# Revit family: 879-100X99-001-DN50-600
name_source: partatom
category: Pipe Accessories
units: mm (PartAtom-declared; Revit-internal decimal feet)

## family parameters
Always vertical = Yes
Cut with Voids When Loaded = No
Part Type = Valve - Breaks Into
Round Connector Dimension = Use Diameter
Shared = No
Work Plane-Based = No

## types (42) — shared parameters
879-0065-10-14400059999 = DN65_PN10/16
879-0065-10-144000599A0 = DN65_PN10/16
879-0080-10-14400059999 = DN80_PN10/16
879-0080-10-144000599A0 = DN80_PN10/16
879-0100-10-14400059999 = DN100_PN10/16
879-0100-10-144000599A0 = DN100_PN10/16
879-0150-10-14400059999 = DN150_PN10/16
879-0150-10-144000599A0 = DN150_PN10/16
879-0200-10-04400059999 = DN200_PN10
879-0200-10-044000599A0 = DN200_PN10
879-0200-10-14400059999 = DN200_PN16
879-0200-10-144000599A0 = DN200_PN16
879-0250-10-04400059999 = DN250_PN10
879-0250-10-044000599A0 = DN250_PN10
879-0250-10-14400059999 = DN250_PN16
879-0250-10-144000599A0 = DN250_PN16
879-0300-10-04400059999 = DN300_PN10
879-0300-10-044000599A0 = DN300_PN10
879-0300-10-14400059999 = DN300_PN16
879-0300-10-144000599A0 = DN300_PN16
879-0350-10-04400059999 = DN350_PN10
879-0350-10-044000599A0 = DN350_PN10
879-0350-10-14400059999 = DN350_PN16
879-0350-10-144000599A0 = DN350_PN16
879-0400-10-04400059999 = DN400_PN10
879-0400-10-044000599A0 = DN400_PN10
879-0400-10-14400059999 = DN400_PN16
879-0400-10-144000599A0 = DN400_PN16
879-0450-10-04400059999 = DN450_PN10
879-0450-10-044000599A0 = DN450_PN10
879-0450-10-14400059999 = DN450_PN16
879-0450-10-144000599A0 = DN450_PN16
879-0500-10-04400059999 = DN500_PN10
879-0500-10-044000599A0 = DN500_PN10
879-0500-10-14400059999 = DN500_PN16
879-0500-10-144000599A0 = DN500_PN16
879-0600-10-04400059999 = DN600_PN10
879-0600-10-044000599A0 = DN600_PN10
879-0600-10-14400059999 = DN600_PN16
879-0600-10-144000599A0 = DN600_PN16
Body_wall_thickness = 10 mm  [stored 0.0328084 ft]
Description_ = AVK PRESSURE REDUCING CONTROL VALVE
Search_Table = 879-100X99-001-DN50-600
URL product pages = https://www.avkvalves.com

## per-type parameters (varying)
- 879-0065-10-14400059999_DN65_PN10/16: 879-0050-10-14400059999=DN50_PN10/16; 879-0050-10-144000599A0=DN50_PN10/16; Body_Collar_Dia=30 mm  [stored 0.0984252 ft]; Body_Collar_Dia_2=26 mm; Body_Flange_Dia=94 mm; Body_Flange_Dia_2=104 mm; Body_Height_1=73 mm; Body_Height_2=36 mm  [stored 0.11811 ft]; Body_Height_3=58 mm; Body_Height_4=51 mm; Body_Top_Dia=13 mm; Body_Top_Dia_2=11 mm; Body_With_Dia=73 mm; Body_With_Dia_2=78 mm; Bolt_support=193 mm; Bolt_support_2=97 mm; Bolt_support_Dia=12 mm  [stored 0.0393701 ft]; Bolt_support_lenght=53 mm; Bolt_support_lenght_2=63 mm; Bottom_profile=16 mm  [stored 0.0524934 ft]; D1=59 mm; D3=93 mm; DN=65 mm; Fillet_Length=6 mm  [stored 0.019685 ft]; Flange_thickness=19 mm  [stored 0.062336 ft]; H3=395 mm; ID=33 mm; L=290 mm; PG_Dia=33 mm; PG_Ref=48 mm; PG_depth=8 mm  [stored 0.0262467 ft]; PG_ref=43 mm; Pilot_Dia_1=18 mm; Pilot_Dia_2=35 mm  [stored 0.114829 ft]; Pilot_Dia_3=12 mm  [stored 0.0393701 ft]; Pilot_Dia_4=6 mm  [stored 0.019685 ft]; Pilot_Dia_5=4 mm  [stored 0.0131234 ft]; Pilot_top_1=252 mm; Pilot_top_ref=50 mm; Profile1_Height=152 mm; Profile1_Length=25 mm  [stored 0.082021 ft]; Profile1_Length_2=17 mm; Profile_Dia=6 mm  [stored 0.019685 ft]; Profile_Dia_2=6 mm  [stored 0.019685 ft]; Profile_Dia_3=12 mm  [stored 0.0393701 ft]; Top_Profile=116 mm; Top_Profile_Ref=121 mm; W=285 mm; W_Ref=281 mm
- 879-0065-10-144000599A0_DN65_PN10/16: 879-0050-10-14400059999=DN50_PN10/16; 879-0050-10-144000599A0=DN50_PN10/16; Body_Collar_Dia=30 mm  [stored 0.0984252 ft]; Body_Collar_Dia_2=26 mm; Body_Flange_Dia=94 mm; Body_Flange_Dia_2=104 mm; Body_Height_1=73 mm; Body_Height_2=36 mm  [stored 0.11811 ft]; Body_Height_3=73 mm; Body_Height_4=51 mm; Body_Top_Dia=13 mm; Body_Top_Dia_2=11 mm; Body_With_Dia=73 mm; Body_With_Dia_2=78 mm; Bolt_support=193 mm; Bolt_support_2=97 mm; Bolt_support_Dia=12 mm  [stored 0.0393701 ft]; Bolt_support_lenght=53 mm; Bolt_support_lenght_2=63 mm; Bottom_profile=16 mm  [stored 0.0524934 ft]; D1=59 mm; D3=93 mm; DN=65 mm; Fillet_Length=6 mm  [stored 0.019685 ft]; Flange_thickness=19 mm  [stored 0.062336 ft]; H3=436 mm; ID=33 mm; L=290 mm; PG_Dia=33 mm; PG_Ref=48 mm; PG_depth=8 mm  [stored 0.0262467 ft]; PG_ref=43 mm; Pilot_Dia_1=18 mm; Pilot_Dia_2=35 mm  [stored 0.114829 ft]; Pilot_Dia_3=12 mm  [stored 0.0393701 ft]; Pilot_Dia_4=6 mm  [stored 0.019685 ft]; Pilot_Dia_5=4 mm  [stored 0.0131234 ft]; Pilot_top_1=280 mm; Pilot_top_ref=64 mm; Profile1_Height=170 mm; Profile1_Length=25 mm  [stored 0.082021 ft]; Profile1_Length_2=17 mm; Profile_Dia=6 mm  [stored 0.019685 ft]; Profile_Dia_2=6 mm  [stored 0.019685 ft]; Profile_Dia_3=12 mm  [stored 0.0393701 ft]; Top_Profile=116 mm; Top_Profile_Ref=121 mm; W=285 mm; W_Ref=281 mm
- 879-0080-10-14400059999_DN80_PN10/16: 879-0050-10-14400059999=DN50_PN10/16; 879-0050-10-144000599A0=DN50_PN10/16; Body_Collar_Dia=32 mm; Body_Collar_Dia_2=28 mm  [stored 0.0918635 ft]; Body_Flange_Dia=100 mm; Body_Flange_Dia_2=111 mm; Body_Height_1=78 mm; Body_Height_2=39 mm  [stored 0.127953 ft]; Body_Height_3=62 mm; Body_Height_4=54 mm; Body_Top_Dia=14 mm  [stored 0.0459318 ft]; Body_Top_Dia_2=12 mm  [stored 0.0393701 ft]; Body_With_Dia=78 mm; Body_With_Dia_2=84 mm; Bolt_support=207 mm; Bolt_support_2=103 mm; Bolt_support_Dia=12 mm  [stored 0.0393701 ft]; Bolt_support_lenght=60 mm; Bolt_support_lenght_2=70 mm; Bottom_profile=20 mm  [stored 0.0656168 ft]; D1=66 mm; D3=100 mm; DN=80 mm; Fillet_Length=6 mm  [stored 0.019685 ft]; Flange_thickness=19 mm  [stored 0.062336 ft]; H3=410 mm; ID=40 mm  [stored 0.131234 ft]; L=310 mm; PG_Dia=40 mm  [stored 0.131234 ft]; PG_Ref=52 mm; PG_depth=8 mm  [stored 0.0262467 ft]; PG_ref=50 mm; Pilot_Dia_1=20 mm  [stored 0.0656168 ft]; Pilot_Dia_2=39 mm  [stored 0.127953 ft]; Pilot_Dia_3=13 mm; Pilot_Dia_4=7 mm; Pilot_Dia_5=4 mm  [stored 0.0131234 ft]; Pilot_top_1=262 mm; Pilot_top_ref=48 mm; Profile1_Height=179 mm; Profile1_Length=27 mm  [stored 0.0885827 ft]; Profile1_Length_2=18 mm; Profile_Dia=6 mm  [stored 0.019685 ft]; Profile_Dia_2=6 mm  [stored 0.019685 ft]; Profile_Dia_3=12 mm  [stored 0.0393701 ft]; Top_Profile=124 mm; Top_Profile_Ref=129 mm; W=300 mm; W_Ref=296 mm
- 879-0080-10-144000599A0_DN80_PN10/16: 879-0050-10-14400059999=DN50_PN10/16; 879-0050-10-144000599A0=DN50_PN10/16; Body_Collar_Dia=32 mm; Body_Collar_Dia_2=28 mm  [stored 0.0918635 ft]; Body_Flange_Dia=100 mm; Body_Flange_Dia_2=111 mm; Body_Height_1=78 mm; Body_Height_2=39 mm  [stored 0.127953 ft]; Body_Height_3=78 mm; Body_Height_4=54 mm; Body_Top_Dia=14 mm  [stored 0.0459318 ft]; Body_Top_Dia_2=12 mm  [stored 0.0393701 ft]; Body_With_Dia=78 mm; Body_With_Dia_2=84 mm; Bolt_support=207 mm; Bolt_support_2=103 mm; Bolt_support_Dia=12 mm  [stored 0.0393701 ft]; Bolt_support_lenght=60 mm; Bolt_support_lenght_2=70 mm; Bottom_profile=20 mm  [stored 0.0656168 ft]; D1=66 mm; D3=100 mm; DN=80 mm; Fillet_Length=6 mm  [stored 0.019685 ft]; Flange_thickness=19 mm  [stored 0.062336 ft]; H3=451 mm; ID=40 mm  [stored 0.131234 ft]; L=310 mm; PG_Dia=40 mm  [stored 0.131234 ft]; PG_Ref=52 mm; PG_depth=8 mm  [stored 0.0262467 ft]; PG_ref=50 mm; Pilot_Dia_1=20 mm  [stored 0.0656168 ft]; Pilot_Dia_2=39 mm  [stored 0.127953 ft]; Pilot_Dia_3=13 mm; Pilot_Dia_4=7 mm; Pilot_Dia_5=4 mm  [stored 0.0131234 ft]; Pilot_top_1=290 mm; Pilot_top_ref=61 mm; Profile1_Height=168 mm; Profile1_Length=27 mm  [stored 0.0885827 ft]; Profile1_Length_2=18 mm; Profile_Dia=6 mm  [stored 0.019685 ft]; Profile_Dia_2=6 mm  [stored 0.019685 ft]; Profile_Dia_3=12 mm  [stored 0.0393701 ft]; Top_Profile=124 mm; Top_Profile_Ref=129 mm; W=300 mm; W_Ref=296 mm
- 879-0100-10-14400059999_DN100_PN10/16: 879-0050-10-14400059999=DN50_PN10/16; 879-0050-10-144000599A0=DN50_PN10/16; Body_Collar_Dia=36 mm  [stored 0.11811 ft]; Body_Collar_Dia_2=31 mm  [stored 0.101706 ft]; Body_Flange_Dia=113 mm; Body_Flange_Dia_2=125 mm; Body_Height_1=88 mm; Body_Height_2=44 mm; Body_Height_3=59 mm; Body_Height_4=59 mm; Body_Top_Dia=16 mm  [stored 0.0524934 ft]; Body_Top_Dia_2=13 mm; Body_With_Dia=88 mm; Body_With_Dia_2=95 mm; Bolt_support=233 mm; Bolt_support_2=117 mm; Bolt_support_Dia=12 mm  [stored 0.0393701 ft]; Bolt_support_lenght=70 mm; Bolt_support_lenght_2=80 mm; Bottom_profile=25 mm  [stored 0.082021 ft]; D1=78 mm; D3=110 mm; DN=100 mm; Fillet_Length=6 mm  [stored 0.019685 ft]; Flange_thickness=19 mm  [stored 0.062336 ft]; H3=430 mm; ID=50 mm; L=350 mm; PG_Dia=50 mm; PG_Ref=58 mm; PG_depth=8 mm  [stored 0.0262467 ft]; PG_ref=60 mm; Pilot_Dia_1=22 mm  [stored 0.0721785 ft]; Pilot_Dia_2=44 mm; Pilot_Dia_3=15 mm  [stored 0.0492126 ft]; Pilot_Dia_4=7 mm; Pilot_Dia_5=5 mm  [stored 0.0164042 ft]; Pilot_top_1=272 mm; Pilot_top_ref=48 mm; Profile1_Height=185 mm; Profile1_Length=30 mm  [stored 0.0984252 ft]; Profile1_Length_2=20 mm  [stored 0.0656168 ft]; Profile_Dia=6 mm  [stored 0.019685 ft]; Profile_Dia_2=6 mm  [stored 0.019685 ft]; Profile_Dia_3=12 mm  [stored 0.0393701 ft]; Top_Profile=140 mm; Top_Profile_Ref=145 mm; W=320 mm; W_Ref=316 mm
- 879-0100-10-144000599A0_DN100_PN10/16: 879-0050-10-14400059999=DN50_PN10/16; 879-0050-10-144000599A0=DN50_PN10/16; Body_Collar_Dia=36 mm  [stored 0.11811 ft]; Body_Collar_Dia_2=31 mm  [stored 0.101706 ft]; Body_Flange_Dia=113 mm; Body_Flange_Dia_2=125 mm; Body_Height_1=88 mm; Body_Height_2=44 mm; Body_Height_3=70 mm; Body_Height_4=59 mm; Body_Top_Dia=16 mm  [stored 0.0524934 ft]; Body_Top_Dia_2=13 mm; Body_With_Dia=88 mm; Body_With_Dia_2=95 mm; Bolt_support=233 mm; Bolt_support_2=117 mm; Bolt_support_Dia=12 mm  [stored 0.0393701 ft]; Bolt_support_lenght=70 mm; Bolt_support_lenght_2=80 mm; Bottom_profile=25 mm  [stored 0.082021 ft]; D1=78 mm; D3=110 mm; DN=100 mm; Fillet_Length=6 mm  [stored 0.019685 ft]; Flange_thickness=19 mm  [stored 0.062336 ft]; H3=474 mm; ID=50 mm; L=350 mm; PG_Dia=50 mm; PG_Ref=58 mm; PG_depth=8 mm  [stored 0.0262467 ft]; PG_ref=60 mm; Pilot_Dia_1=22 mm  [stored 0.0721785 ft]; Pilot_Dia_2=44 mm; Pilot_Dia_3=15 mm  [stored 0.0492126 ft]; Pilot_Dia_4=7 mm; Pilot_Dia_5=5 mm  [stored 0.0164042 ft]; Pilot_top_1=300 mm; Pilot_top_ref=64 mm; Profile1_Height=176 mm; Profile1_Length=30 mm  [stored 0.0984252 ft]; Profile1_Length_2=20 mm  [stored 0.0656168 ft]; Profile_Dia=6 mm  [stored 0.019685 ft]; Profile_Dia_2=6 mm  [stored 0.019685 ft]; Profile_Dia_3=12 mm  [stored 0.0393701 ft]; Top_Profile=140 mm; Top_Profile_Ref=145 mm; W=320 mm; W_Ref=316 mm
- 879-0150-10-14400059999_DN150_PN10/16: 879-0050-10-14400059999=DN50_PN10/16; 879-0050-10-144000599A0=DN50_PN10/16; Body_Collar_Dia=50 mm; Body_Collar_Dia_2=43 mm; Body_Flange_Dia=155 mm; Body_Flange_Dia_2=171 mm; Body_Height_1=120 mm; Body_Height_2=60 mm; Body_Height_3=60 mm; Body_Height_4=75 mm; Body_Top_Dia=22 mm  [stored 0.0721785 ft]; Body_Top_Dia_2=18 mm; Body_With_Dia=120 mm; Body_With_Dia_2=130 mm; Bolt_support=320 mm; Bolt_support_2=160 mm; Bolt_support_Dia=16 mm  [stored 0.0524934 ft]; Bolt_support_lenght=95 mm; Bolt_support_lenght_2=105 mm; Bottom_profile=38 mm; D1=106 mm; D3=143 mm; DN=150 mm; Fillet_Length=8 mm  [stored 0.0262467 ft]; Flange_thickness=19 mm  [stored 0.062336 ft]; H3=575 mm; ID=75 mm; L=480 mm; PG_Dia=50 mm; PG_Ref=80 mm; PG_depth=11 mm; PG_ref=85 mm; Pilot_Dia_1=31 mm  [stored 0.101706 ft]; Pilot_Dia_2=62 mm; Pilot_Dia_3=21 mm  [stored 0.0688976 ft]; Pilot_Dia_4=10 mm  [stored 0.0328084 ft]; Pilot_Dia_5=7 mm; Pilot_top_1=354 mm; Pilot_top_ref=79 mm; Profile1_Height=230 mm; Profile1_Length=39 mm  [stored 0.127953 ft]; Profile1_Length_2=26 mm; Profile_Dia=8 mm  [stored 0.0262467 ft]; Profile_Dia_2=8 mm  [stored 0.0262467 ft]; Profile_Dia_3=16 mm  [stored 0.0524934 ft]; Top_Profile=192 mm; Top_Profile_Ref=197 mm; W=385 mm; W_Ref=379 mm
- 879-0150-10-144000599A0_DN150_PN10/16: 879-0050-10-14400059999=DN50_PN10/16; 879-0050-10-144000599A0=DN50_PN10/16; Body_Collar_Dia=50 mm; Body_Collar_Dia_2=43 mm; Body_Flange_Dia=155 mm; Body_Flange_Dia_2=171 mm; Body_Height_1=120 mm; Body_Height_2=60 mm; Body_Height_3=68 mm; Body_Height_4=75 mm; Body_Top_Dia=22 mm  [stored 0.0721785 ft]; Body_Top_Dia_2=18 mm; Body_With_Dia=120 mm; Body_With_Dia_2=130 mm; Bolt_support=320 mm; Bolt_support_2=160 mm; Bolt_support_Dia=16 mm  [stored 0.0524934 ft]; Bolt_support_lenght=95 mm; Bolt_support_lenght_2=105 mm; Bottom_profile=38 mm; D1=106 mm; D3=143 mm; DN=150 mm; Fillet_Length=8 mm  [stored 0.0262467 ft]; Flange_thickness=19 mm  [stored 0.062336 ft]; H3=607 mm; ID=75 mm; L=480 mm; PG_Dia=50 mm; PG_Ref=80 mm; PG_depth=11 mm; PG_ref=85 mm; Pilot_Dia_1=31 mm  [stored 0.101706 ft]; Pilot_Dia_2=62 mm; Pilot_Dia_3=21 mm  [stored 0.0688976 ft]; Pilot_Dia_4=10 mm  [stored 0.0328084 ft]; Pilot_Dia_5=7 mm; Pilot_top_1=374 mm; Pilot_top_ref=91 mm; Profile1_Height=230 mm; Profile1_Length=39 mm  [stored 0.127953 ft]; Profile1_Length_2=26 mm; Profile_Dia=8 mm  [stored 0.0262467 ft]; Profile_Dia_2=8 mm  [stored 0.0262467 ft]; Profile_Dia_3=16 mm  [stored 0.0524934 ft]; Top_Profile=192 mm; Top_Profile_Ref=197 mm; W=385 mm; W_Ref=379 mm
- 879-0200-10-04400059999_DN200_PN10: 879-0050-10-14400059999=DN50_PN10/16; 879-0050-10-144000599A0=DN50_PN10/16; Body_Collar_Dia=63 mm; Body_Collar_Dia_2=54 mm; Body_Flange_Dia=194 mm; Body_Flange_Dia_2=214 mm; Body_Height_1=150 mm; Body_Height_2=75 mm; Body_Height_3=75 mm; Body_Height_4=90 mm; Body_Top_Dia=27 mm  [stored 0.0885827 ft]; Body_Top_Dia_2=22 mm  [stored 0.0721785 ft]; Body_With_Dia=150 mm; Body_With_Dia_2=162 mm; Bolt_support=400 mm; Bolt_support_2=200 mm; Bolt_support_Dia=20 mm  [stored 0.0656168 ft]; Bolt_support_lenght=120 mm; Bolt_support_lenght_2=130 mm; Bottom_profile=50 mm; D1=133 mm; D3=170 mm; DN=200 mm; Fillet_Length=10 mm  [stored 0.0328084 ft]; Flange_thickness=20 mm  [stored 0.0656168 ft]; H3=690 mm; ID=100 mm; L=600 mm; PG_Dia=67 mm; PG_Ref=100 mm; PG_depth=14 mm  [stored 0.0459318 ft]; PG_ref=110 mm; Pilot_Dia_1=39 mm  [stored 0.127953 ft]; Pilot_Dia_2=77 mm; Pilot_Dia_3=26 mm; Pilot_Dia_4=13 mm; Pilot_Dia_5=9 mm  [stored 0.0295276 ft]; Pilot_top_1=428 mm; Pilot_top_ref=93 mm; Profile1_Height=273 mm; Profile1_Length=46 mm; Profile1_Length_2=31 mm  [stored 0.101706 ft]; Profile_Dia=10 mm  [stored 0.0328084 ft]; Profile_Dia_2=10 mm  [stored 0.0328084 ft]; Profile_Dia_3=20 mm  [stored 0.0656168 ft]; Top_Profile=240 mm; Top_Profile_Ref=245 mm; W=420 mm; W_Ref=413 mm
- 879-0200-10-044000599A0_DN200_PN10: 879-0050-10-14400059999=DN50_PN10/16; 879-0050-10-144000599A0=DN50_PN10/16; Body_Collar_Dia=63 mm; Body_Collar_Dia_2=54 mm; Body_Flange_Dia=194 mm; Body_Flange_Dia_2=214 mm; Body_Height_1=150 mm; Body_Height_2=75 mm; Body_Height_3=100 mm; Body_Height_4=90 mm; Body_Top_Dia=27 mm  [stored 0.0885827 ft]; Body_Top_Dia_2=22 mm  [stored 0.0721785 ft]; Body_With_Dia=150 mm; Body_With_Dia_2=162 mm; Bolt_support=400 mm; Bolt_support_2=200 mm; Bolt_support_Dia=20 mm  [stored 0.0656168 ft]; Bolt_support_lenght=120 mm; Bolt_support_lenght_2=130 mm; Bottom_profile=50 mm; D1=133 mm; D3=170 mm; DN=200 mm; Fillet_Length=10 mm  [stored 0.0328084 ft]; Flange_thickness=20 mm  [stored 0.0656168 ft]; H3=774 mm; ID=100 mm; L=600 mm; PG_Dia=67 mm; PG_Ref=100 mm; PG_depth=14 mm  [stored 0.0459318 ft]; PG_ref=110 mm; Pilot_Dia_1=39 mm  [stored 0.127953 ft]; Pilot_Dia_2=77 mm; Pilot_Dia_3=26 mm; Pilot_Dia_4=13 mm; Pilot_Dia_5=9 mm  [stored 0.0295276 ft]; Pilot_top_1=482 mm; Pilot_top_ref=122 mm; Profile1_Height=275 mm; Profile1_Length=46 mm; Profile1_Length_2=31 mm  [stored 0.101706 ft]; Profile_Dia=10 mm  [stored 0.0328084 ft]; Profile_Dia_2=10 mm  [stored 0.0328084 ft]; Profile_Dia_3=20 mm  [stored 0.0656168 ft]; Top_Profile=240 mm; Top_Profile_Ref=245 mm; W=420 mm; W_Ref=413 mm
- 879-0200-10-14400059999_DN200_PN16: 879-0050-10-14400059999=DN50_PN10/16; 879-0050-10-144000599A0=DN50_PN10/16; Body_Collar_Dia=63 mm; Body_Collar_Dia_2=54 mm; Body_Flange_Dia=194 mm; Body_Flange_Dia_2=214 mm; Body_Height_1=150 mm; Body_Height_2=75 mm; Body_Height_3=75 mm; Body_Height_4=90 mm; Body_Top_Dia=27 mm  [stored 0.0885827 ft]; Body_Top_Dia_2=22 mm  [stored 0.0721785 ft]; Body_With_Dia=150 mm; Body_With_Dia_2=162 mm; Bolt_support=400 mm; Bolt_support_2=200 mm; Bolt_support_Dia=20 mm  [stored 0.0656168 ft]; Bolt_support_lenght=120 mm; Bolt_support_lenght_2=130 mm; Bottom_profile=50 mm; D1=133 mm; D3=170 mm; DN=200 mm; Fillet_Length=10 mm  [stored 0.0328084 ft]; Flange_thickness=20 mm  [stored 0.0656168 ft]; H3=690 mm; ID=100 mm; L=600 mm; PG_Dia=67 mm; PG_Ref=100 mm; PG_depth=14 mm  [stored 0.0459318 ft]; PG_ref=110 mm; Pilot_Dia_1=39 mm  [stored 0.127953 ft]; Pilot_Dia_2=77 mm; Pilot_Dia_3=26 mm; Pilot_Dia_4=13 mm; Pilot_Dia_5=9 mm  [stored 0.0295276 ft]; Pilot_top_1=428 mm; Pilot_top_ref=93 mm; Profile1_Height=273 mm; Profile1_Length=46 mm; Profile1_Length_2=31 mm  [stored 0.101706 ft]; Profile_Dia=10 mm  [stored 0.0328084 ft]; Profile_Dia_2=10 mm  [stored 0.0328084 ft]; Profile_Dia_3=20 mm  [stored 0.0656168 ft]; Top_Profile=240 mm; Top_Profile_Ref=245 mm; W=420 mm; W_Ref=413 mm
- 879-0200-10-144000599A0_DN200_PN16: 879-0050-10-14400059999=DN50_PN10/16; 879-0050-10-144000599A0=DN50_PN10/16; Body_Collar_Dia=63 mm; Body_Collar_Dia_2=54 mm; Body_Flange_Dia=194 mm; Body_Flange_Dia_2=214 mm; Body_Height_1=150 mm; Body_Height_2=75 mm; Body_Height_3=86 mm; Body_Height_4=90 mm; Body_Top_Dia=27 mm  [stored 0.0885827 ft]; Body_Top_Dia_2=22 mm  [stored 0.0721785 ft]; Body_With_Dia=150 mm; Body_With_Dia_2=162 mm; Bolt_support=400 mm; Bolt_support_2=200 mm; Bolt_support_Dia=20 mm  [stored 0.0656168 ft]; Bolt_support_lenght=120 mm; Bolt_support_lenght_2=130 mm; Bottom_profile=50 mm; D1=133 mm; D3=170 mm; DN=200 mm; Fillet_Length=10 mm  [stored 0.0328084 ft]; Flange_thickness=20 mm  [stored 0.0656168 ft]; H3=774 mm; ID=100 mm; L=600 mm; PG_Dia=67 mm; PG_Ref=100 mm; PG_depth=14 mm  [stored 0.0459318 ft]; PG_ref=110 mm; Pilot_Dia_1=39 mm  [stored 0.127953 ft]; Pilot_Dia_2=77 mm; Pilot_Dia_3=26 mm; Pilot_Dia_4=13 mm; Pilot_Dia_5=9 mm  [stored 0.0295276 ft]; Pilot_top_1=475 mm; Pilot_top_ref=129 mm; Profile1_Height=275 mm; Profile1_Length=46 mm; Profile1_Length_2=31 mm  [stored 0.101706 ft]; Profile_Dia=10 mm  [stored 0.0328084 ft]; Profile_Dia_2=10 mm  [stored 0.0328084 ft]; Profile_Dia_3=20 mm  [stored 0.0656168 ft]; Top_Profile=240 mm; Top_Profile_Ref=245 mm; W=420 mm; W_Ref=413 mm
- 879-0250-10-04400059999_DN250_PN10: 879-0050-10-14400059999=DN50_PN10/16; 879-0050-10-144000599A0=DN50_PN10/16; Body_Collar_Dia=76 mm; Body_Collar_Dia_2=65 mm; Body_Flange_Dia=235 mm; Body_Flange_Dia_2=261 mm; Body_Height_1=183 mm; Body_Height_2=91 mm; Body_Height_3=81 mm; Body_Height_4=106 mm; Body_Top_Dia=33 mm; Body_Top_Dia_2=27 mm  [stored 0.0885827 ft]; Body_With_Dia=183 mm; Body_With_Dia_2=197 mm; Bolt_support=487 mm; Bolt_support_2=243 mm; Bolt_support_Dia=20 mm  [stored 0.0656168 ft]; Bolt_support_lenght=145 mm; Bolt_support_lenght_2=155 mm; Bottom_profile=63 mm; D1=160 mm; D3=198 mm; DN=250 mm; Fillet_Length=10 mm  [stored 0.0328084 ft]; Flange_thickness=22 mm  [stored 0.0721785 ft]; H3=770 mm; ID=125 mm; L=730 mm; PG_Dia=83 mm; PG_Ref=122 mm; PG_depth=14 mm  [stored 0.0459318 ft]; PG_ref=135 mm; Pilot_Dia_1=46 mm; Pilot_Dia_2=92 mm; Pilot_Dia_3=31 mm  [stored 0.101706 ft]; Pilot_Dia_4=15 mm  [stored 0.0492126 ft]; Pilot_Dia_5=10 mm  [stored 0.0328084 ft]; Pilot_top_1=481 mm; Pilot_top_ref=91 mm; Profile1_Height=327 mm; Profile1_Length=53 mm; Profile1_Length_2=36 mm  [stored 0.11811 ft]; Profile_Dia=10 mm  [stored 0.0328084 ft]; Profile_Dia_2=10 mm  [stored 0.0328084 ft]; Profile_Dia_3=20 mm  [stored 0.0656168 ft]; Top_Profile=292 mm; Top_Profile_Ref=297 mm; W=485 mm; W_Ref=478 mm
- 879-0250-10-044000599A0_DN250_PN10: 879-0050-10-14400059999=DN50_PN10/16; 879-0050-10-144000599A0=DN50_PN10/16; Body_Collar_Dia=76 mm; Body_Collar_Dia_2=65 mm; Body_Flange_Dia=235 mm; Body_Flange_Dia_2=261 mm; Body_Height_1=183 mm; Body_Height_2=91 mm; Body_Height_3=105 mm; Body_Height_4=106 mm; Body_Top_Dia=33 mm; Body_Top_Dia_2=27 mm  [stored 0.0885827 ft]; Body_With_Dia=183 mm; Body_With_Dia_2=197 mm; Bolt_support=487 mm; Bolt_support_2=243 mm; Bolt_support_Dia=20 mm  [stored 0.0656168 ft]; Bolt_support_lenght=145 mm; Bolt_support_lenght_2=155 mm; Bottom_profile=63 mm; D1=160 mm; D3=198 mm; DN=250 mm; Fillet_Length=10 mm  [stored 0.0328084 ft]; Flange_thickness=22 mm  [stored 0.0721785 ft]; H3=854 mm; ID=125 mm; L=730 mm; PG_Dia=83 mm; PG_Ref=122 mm; PG_depth=14 mm  [stored 0.0459318 ft]; PG_ref=135 mm; Pilot_Dia_1=46 mm; Pilot_Dia_2=92 mm; Pilot_Dia_3=31 mm  [stored 0.101706 ft]; Pilot_Dia_4=15 mm  [stored 0.0492126 ft]; Pilot_Dia_5=10 mm  [stored 0.0328084 ft]; Pilot_top_1=535 mm; Pilot_top_ref=122 mm; Profile1_Height=330 mm; Profile1_Length=53 mm; Profile1_Length_2=36 mm  [stored 0.11811 ft]; Profile_Dia=10 mm  [stored 0.0328084 ft]; Profile_Dia_2=10 mm  [stored 0.0328084 ft]; Profile_Dia_3=20 mm  [stored 0.0656168 ft]; Top_Profile=292 mm; Top_Profile_Ref=297 mm; W=485 mm; W_Ref=478 mm
- 879-0250-10-14400059999_DN250_PN16: 879-0050-10-14400059999=DN50_PN10/16; 879-0050-10-144000599A0=DN50_PN10/16; Body_Collar_Dia=76 mm; Body_Collar_Dia_2=65 mm; Body_Flange_Dia=235 mm; Body_Flange_Dia_2=261 mm; Body_Height_1=183 mm; Body_Height_2=91 mm; Body_Height_3=81 mm; Body_Height_4=106 mm; Body_Top_Dia=33 mm; Body_Top_Dia_2=27 mm  [stored 0.0885827 ft]; Body_With_Dia=183 mm; Body_With_Dia_2=197 mm; Bolt_support=487 mm; Bolt_support_2=243 mm; Bolt_support_Dia=20 mm  [stored 0.0656168 ft]; Bolt_support_lenght=145 mm; Bolt_support_lenght_2=155 mm; Bottom_profile=63 mm; D1=160 mm; D3=203 mm; DN=250 mm; Fillet_Length=10 mm  [stored 0.0328084 ft]; Flange_thickness=22 mm  [stored 0.0721785 ft]; H3=770 mm; ID=125 mm; L=730 mm; PG_Dia=83 mm; PG_Ref=122 mm; PG_depth=14 mm  [stored 0.0459318 ft]; PG_ref=135 mm; Pilot_Dia_1=47 mm; Pilot_Dia_2=94 mm; Pilot_Dia_3=31 mm  [stored 0.101706 ft]; Pilot_Dia_4=16 mm  [stored 0.0524934 ft]; Pilot_Dia_5=10 mm  [stored 0.0328084 ft]; Pilot_top_1=479 mm; Pilot_top_ref=89 mm; Profile1_Height=335 mm; Profile1_Length=55 mm; Profile1_Length_2=36 mm  [stored 0.11811 ft]; Profile_Dia=10 mm  [stored 0.0328084 ft]; Profile_Dia_2=10 mm  [stored 0.0328084 ft]; Profile_Dia_3=20 mm  [stored 0.0656168 ft]; Top_Profile=292 mm; Top_Profile_Ref=297 mm; W=485 mm; W_Ref=478 mm
- 879-0250-10-144000599A0_DN250_PN16: 879-0050-10-14400059999=DN50_PN10/16; 879-0050-10-144000599A0=DN50_PN10/16; Body_Collar_Dia=76 mm; Body_Collar_Dia_2=65 mm; Body_Flange_Dia=235 mm; Body_Flange_Dia_2=261 mm; Body_Height_1=183 mm; Body_Height_2=91 mm; Body_Height_3=81 mm; Body_Height_4=106 mm; Body_Top_Dia=33 mm; Body_Top_Dia_2=27 mm  [stored 0.0885827 ft]; Body_With_Dia=183 mm; Body_With_Dia_2=197 mm; Bolt_support=487 mm; Bolt_support_2=243 mm; Bolt_support_Dia=20 mm  [stored 0.0656168 ft]; Bolt_support_lenght=145 mm; Bolt_support_lenght_2=155 mm; Bottom_profile=63 mm; D1=160 mm; D3=203 mm; DN=250 mm; Fillet_Length=10 mm  [stored 0.0328084 ft]; Flange_thickness=22 mm  [stored 0.0721785 ft]; H3=854 mm; ID=125 mm; L=730 mm; PG_Dia=83 mm; PG_Ref=122 mm; PG_depth=14 mm  [stored 0.0459318 ft]; PG_ref=135 mm; Pilot_Dia_1=47 mm; Pilot_Dia_2=94 mm; Pilot_Dia_3=31 mm  [stored 0.101706 ft]; Pilot_Dia_4=16 mm  [stored 0.0524934 ft]; Pilot_Dia_5=10 mm  [stored 0.0328084 ft]; Pilot_top_1=521 mm; Pilot_top_ref=131 mm; Profile1_Height=350 mm; Profile1_Length=55 mm; Profile1_Length_2=36 mm  [stored 0.11811 ft]; Profile_Dia=10 mm  [stored 0.0328084 ft]; Profile_Dia_2=10 mm  [stored 0.0328084 ft]; Profile_Dia_3=20 mm  [stored 0.0656168 ft]; Top_Profile=292 mm; Top_Profile_Ref=297 mm; W=485 mm; W_Ref=478 mm
- 879-0300-10-04400059999_DN300_PN10: 879-0050-10-14400059999=DN50_PN10/16; 879-0050-10-144000599A0=DN50_PN10/16; Body_Collar_Dia=89 mm; Body_Collar_Dia_2=76 mm; Body_Flange_Dia=274 mm; Body_Flange_Dia_2=304 mm; Body_Height_1=213 mm; Body_Height_2=106 mm; Body_Height_3=95 mm; Body_Height_4=121 mm; Body_Top_Dia=38 mm; Body_Top_Dia_2=32 mm; Body_With_Dia=213 mm; Body_With_Dia_2=230 mm; Bolt_support=567 mm; Bolt_support_2=283 mm; Bolt_support_Dia=20 mm  [stored 0.0656168 ft]; Bolt_support_lenght=170 mm; Bolt_support_lenght_2=180 mm; Bottom_profile=75 mm; D1=185 mm; D3=223 mm; DN=300 mm; Fillet_Length=10 mm  [stored 0.0328084 ft]; Flange_thickness=25 mm  [stored 0.082021 ft]; H3=835 mm; ID=150 mm; L=850 mm; PG_Dia=100 mm; PG_Ref=142 mm; PG_depth=14 mm  [stored 0.0459318 ft]; PG_ref=160 mm; Pilot_Dia_1=53 mm; Pilot_Dia_2=105 mm; Pilot_Dia_3=35 mm  [stored 0.114829 ft]; Pilot_Dia_4=18 mm; Pilot_Dia_5=12 mm  [stored 0.0393701 ft]; Pilot_top_1=530 mm; Pilot_top_ref=82 mm; Profile1_Height=361 mm; Profile1_Length=60 mm; Profile1_Length_2=40 mm  [stored 0.131234 ft]; Profile_Dia=10 mm  [stored 0.0328084 ft]; Profile_Dia_2=10 mm  [stored 0.0328084 ft]; Profile_Dia_3=20 mm  [stored 0.0656168 ft]; Top_Profile=340 mm; Top_Profile_Ref=345 mm; W=540 mm; W_Ref=533 mm
- 879-0300-10-044000599A0_DN300_PN10: 879-0050-10-14400059999=DN50_PN10/16; 879-0050-10-144000599A0=DN50_PN10/16; Body_Collar_Dia=89 mm; Body_Collar_Dia_2=76 mm; Body_Flange_Dia=274 mm; Body_Flange_Dia_2=304 mm; Body_Height_1=213 mm; Body_Height_2=106 mm; Body_Height_3=106 mm; Body_Height_4=121 mm; Body_Top_Dia=38 mm; Body_Top_Dia_2=32 mm; Body_With_Dia=213 mm; Body_With_Dia_2=230 mm; Bolt_support=567 mm; Bolt_support_2=283 mm; Bolt_support_Dia=20 mm  [stored 0.0656168 ft]; Bolt_support_lenght=170 mm; Bolt_support_lenght_2=180 mm; Bottom_profile=75 mm; D1=185 mm; D3=223 mm; DN=300 mm; Fillet_Length=10 mm  [stored 0.0328084 ft]; Flange_thickness=25 mm  [stored 0.082021 ft]; H3=923 mm; ID=150 mm; L=850 mm; PG_Dia=100 mm; PG_Ref=142 mm; PG_depth=14 mm  [stored 0.0459318 ft]; PG_ref=160 mm; Pilot_Dia_1=53 mm; Pilot_Dia_2=105 mm; Pilot_Dia_3=35 mm  [stored 0.114829 ft]; Pilot_Dia_4=18 mm; Pilot_Dia_5=12 mm  [stored 0.0393701 ft]; Pilot_top_1=580 mm; Pilot_top_ref=120 mm; Profile1_Height=400 mm; Profile1_Length=60 mm; Profile1_Length_2=40 mm  [stored 0.131234 ft]; Profile_Dia=10 mm  [stored 0.0328084 ft]; Profile_Dia_2=10 mm  [stored 0.0328084 ft]; Profile_Dia_3=20 mm  [stored 0.0656168 ft]; Top_Profile=340 mm; Top_Profile_Ref=345 mm; W=540 mm; W_Ref=533 mm
- 879-0300-10-14400059999_DN300_PN16: 879-0050-10-14400059999=DN50_PN10/16; 879-0050-10-144000599A0=DN50_PN10/16; Body_Collar_Dia=89 mm; Body_Collar_Dia_2=76 mm; Body_Flange_Dia=274 mm; Body_Flange_Dia_2=304 mm; Body_Height_1=213 mm; Body_Height_2=106 mm; Body_Height_3=95 mm; Body_Height_4=121 mm; Body_Top_Dia=38 mm; Body_Top_Dia_2=32 mm; Body_With_Dia=213 mm; Body_With_Dia_2=230 mm; Bolt_support=567 mm; Bolt_support_2=283 mm; Bolt_support_Dia=20 mm  [stored 0.0656168 ft]; Bolt_support_lenght=170 mm; Bolt_support_lenght_2=180 mm; Bottom_profile=75 mm; D1=185 mm; D3=230 mm; DN=300 mm; Fillet_Length=10 mm  [stored 0.0328084 ft]; Flange_thickness=25 mm  [stored 0.082021 ft]; H3=835 mm; ID=150 mm; L=850 mm; PG_Dia=100 mm; PG_Ref=142 mm; PG_depth=14 mm  [stored 0.0459318 ft]; PG_ref=160 mm; Pilot_Dia_1=55 mm; Pilot_Dia_2=109 mm; Pilot_Dia_3=36 mm  [stored 0.11811 ft]; Pilot_Dia_4=18 mm; Pilot_Dia_5=12 mm  [stored 0.0393701 ft]; Pilot_top_1=527 mm; Pilot_top_ref=78 mm; Profile1_Height=380 mm; Profile1_Length=62 mm; Profile1_Length_2=41 mm; Profile_Dia=10 mm  [stored 0.0328084 ft]; Profile_Dia_2=10 mm  [stored 0.0328084 ft]; Profile_Dia_3=20 mm  [stored 0.0656168 ft]; Top_Profile=340 mm; Top_Profile_Ref=345 mm; W=540 mm; W_Ref=533 mm
- 879-0300-10-144000599A0_DN300_PN16: 879-0050-10-14400059999=DN50_PN10/16; 879-0050-10-144000599A0=DN50_PN10/16; Body_Collar_Dia=89 mm; Body_Collar_Dia_2=76 mm; Body_Flange_Dia=274 mm; Body_Flange_Dia_2=304 mm; Body_Height_1=213 mm; Body_Height_2=106 mm; Body_Height_3=95 mm; Body_Height_4=121 mm; Body_Top_Dia=38 mm; Body_Top_Dia_2=32 mm; Body_With_Dia=213 mm; Body_With_Dia_2=230 mm; Bolt_support=567 mm; Bolt_support_2=283 mm; Bolt_support_Dia=20 mm  [stored 0.0656168 ft]; Bolt_support_lenght=170 mm; Bolt_support_lenght_2=180 mm; Bottom_profile=75 mm; D1=185 mm; D3=230 mm; DN=300 mm; Fillet_Length=10 mm  [stored 0.0328084 ft]; Flange_thickness=25 mm  [stored 0.082021 ft]; H3=923 mm; ID=150 mm; L=850 mm; PG_Dia=100 mm; PG_Ref=142 mm; PG_depth=14 mm  [stored 0.0459318 ft]; PG_ref=160 mm; Pilot_Dia_1=55 mm; Pilot_Dia_2=109 mm; Pilot_Dia_3=36 mm  [stored 0.11811 ft]; Pilot_Dia_4=18 mm; Pilot_Dia_5=12 mm  [stored 0.0393701 ft]; Pilot_top_1=571 mm; Pilot_top_ref=122 mm; Profile1_Height=380 mm; Profile1_Length=62 mm; Profile1_Length_2=41 mm; Profile_Dia=10 mm  [stored 0.0328084 ft]; Profile_Dia_2=10 mm  [stored 0.0328084 ft]; Profile_Dia_3=20 mm  [stored 0.0656168 ft]; Top_Profile=340 mm; Top_Profile_Ref=345 mm; W=540 mm; W_Ref=533 mm
- 879-0350-10-04400059999_DN350_PN10: 879-0050-10-14400059999=DN50_PN10/16; 879-0050-10-144000599A0=DN50_PN10/16; Body_Collar_Dia=102 mm; Body_Collar_Dia_2=88 mm; Body_Flange_Dia=316 mm; Body_Flange_Dia_2=350 mm; Body_Height_1=245 mm; Body_Height_2=123 mm; Body_Height_3=98 mm; Body_Height_4=138 mm; Body_Top_Dia=44 mm; Body_Top_Dia_2=37 mm; Body_With_Dia=245 mm; Body_With_Dia_2=265 mm; Bolt_support=653 mm; Bolt_support_2=327 mm; Bolt_support_Dia=30 mm  [stored 0.0984252 ft]; Bolt_support_lenght=195 mm; Bolt_support_lenght_2=205 mm; Bottom_profile=88 mm; D1=215 mm; D3=253 mm; DN=350 mm; Fillet_Length=15 mm  [stored 0.0492126 ft]; Flange_thickness=27 mm  [stored 0.0885827 ft]; H3=960 mm; ID=175 mm; L=980 mm; PG_Dia=117 mm; PG_Ref=163 mm; PG_depth=21 mm  [stored 0.0688976 ft]; PG_ref=185 mm; Pilot_Dia_1=61 mm; Pilot_Dia_2=121 mm; Pilot_Dia_3=40 mm  [stored 0.131234 ft]; Pilot_Dia_4=20 mm  [stored 0.0656168 ft]; Pilot_Dia_5=13 mm; Pilot_top_1=604 mm; Pilot_top_ref=104 mm; Profile1_Height=430 mm; Profile1_Length=68 mm; Profile1_Length_2=45 mm; Profile_Dia=15 mm  [stored 0.0492126 ft]; Profile_Dia_2=15 mm  [stored 0.0492126 ft]; Profile_Dia_3=30 mm  [stored 0.0984252 ft]; Top_Profile=392 mm; Top_Profile_Ref=397 mm; W=600 mm; W_Ref=590 mm
- 879-0350-10-044000599A0_DN350_PN10: 879-0050-10-14400059999=DN50_PN10/16; 879-0050-10-144000599A0=DN50_PN10/16; Body_Collar_Dia=102 mm; Body_Collar_Dia_2=88 mm; Body_Flange_Dia=316 mm; Body_Flange_Dia_2=350 mm; Body_Height_1=245 mm; Body_Height_2=123 mm; Body_Height_3=98 mm; Body_Height_4=138 mm; Body_Top_Dia=44 mm; Body_Top_Dia_2=37 mm; Body_With_Dia=245 mm; Body_With_Dia_2=265 mm; Bolt_support=653 mm; Bolt_support_2=327 mm; Bolt_support_Dia=30 mm  [stored 0.0984252 ft]; Bolt_support_lenght=195 mm; Bolt_support_lenght_2=205 mm; Bottom_profile=88 mm; D1=215 mm; D3=253 mm; DN=350 mm; Fillet_Length=15 mm  [stored 0.0492126 ft]; Flange_thickness=27 mm  [stored 0.0885827 ft]; H3=1045 mm; ID=175 mm; L=980 mm; PG_Dia=117 mm; PG_Ref=163 mm; PG_depth=21 mm  [stored 0.0688976 ft]; PG_ref=185 mm; Pilot_Dia_1=61 mm; Pilot_Dia_2=121 mm; Pilot_Dia_3=40 mm  [stored 0.131234 ft]; Pilot_Dia_4=20 mm  [stored 0.0656168 ft]; Pilot_Dia_5=13 mm; Pilot_top_1=647 mm; Pilot_top_ref=146 mm; Profile1_Height=430 mm; Profile1_Length=68 mm; Profile1_Length_2=45 mm; Profile_Dia=15 mm  [stored 0.0492126 ft]; Profile_Dia_2=15 mm  [stored 0.0492126 ft]; Profile_Dia_3=30 mm  [stored 0.0984252 ft]; Top_Profile=392 mm; Top_Profile_Ref=397 mm; W=600 mm; W_Ref=590 mm
- 879-0350-10-14400059999_DN350_PN16: 879-0050-10-14400059999=DN50_PN10/16; 879-0050-10-144000599A0=DN50_PN10/16; Body_Collar_Dia=102 mm; Body_Collar_Dia_2=88 mm; Body_Flange_Dia=316 mm; Body_Flange_Dia_2=350 mm; Body_Height_1=245 mm; Body_Height_2=123 mm; Body_Height_3=89 mm; Body_Height_4=138 mm; Body_Top_Dia=44 mm; Body_Top_Dia_2=37 mm; Body_With_Dia=245 mm; Body_With_Dia_2=265 mm; Bolt_support=653 mm; Bolt_support_2=327 mm; Bolt_support_Dia=30 mm  [stored 0.0984252 ft]; Bolt_support_lenght=195 mm; Bolt_support_lenght_2=205 mm; Bottom_profile=88 mm; D1=215 mm; D3=260 mm; DN=350 mm; Fillet_Length=15 mm  [stored 0.0492126 ft]; Flange_thickness=27 mm  [stored 0.0885827 ft]; H3=960 mm; ID=175 mm; L=980 mm; PG_Dia=117 mm; PG_Ref=163 mm; PG_depth=21 mm  [stored 0.0688976 ft]; PG_ref=185 mm; Pilot_Dia_1=63 mm; Pilot_Dia_2=126 mm; Pilot_Dia_3=42 mm  [stored 0.137795 ft]; Pilot_Dia_4=21 mm  [stored 0.0688976 ft]; Pilot_Dia_5=14 mm  [stored 0.0459318 ft]; Pilot_top_1=596 mm; Pilot_top_ref=104 mm; Profile1_Height=430 mm; Profile1_Length=70 mm; Profile1_Length_2=47 mm; Profile_Dia=15 mm  [stored 0.0492126 ft]; Profile_Dia_2=15 mm  [stored 0.0492126 ft]; Profile_Dia_3=30 mm  [stored 0.0984252 ft]; Top_Profile=392 mm; Top_Profile_Ref=397 mm; W=600 mm; W_Ref=590 mm
- 879-0350-10-144000599A0_DN350_PN16: 879-0050-10-14400059999=DN50_PN10/16; 879-0050-10-144000599A0=DN50_PN10/16; Body_Collar_Dia=102 mm; Body_Collar_Dia_2=88 mm; Body_Flange_Dia=316 mm; Body_Flange_Dia_2=350 mm; Body_Height_1=245 mm; Body_Height_2=123 mm; Body_Height_3=89 mm; Body_Height_4=138 mm; Body_Top_Dia=44 mm; Body_Top_Dia_2=37 mm; Body_With_Dia=245 mm; Body_With_Dia_2=265 mm; Bolt_support=653 mm; Bolt_support_2=327 mm; Bolt_support_Dia=30 mm  [stored 0.0984252 ft]; Bolt_support_lenght=195 mm; Bolt_support_lenght_2=205 mm; Bottom_profile=88 mm; D1=215 mm; D3=260 mm; DN=350 mm; Fillet_Length=15 mm  [stored 0.0492126 ft]; Flange_thickness=27 mm  [stored 0.0885827 ft]; H3=1045 mm; ID=175 mm; L=980 mm; PG_Dia=117 mm; PG_Ref=163 mm; PG_depth=21 mm  [stored 0.0688976 ft]; PG_ref=185 mm; Pilot_Dia_1=63 mm; Pilot_Dia_2=126 mm; Pilot_Dia_3=42 mm  [stored 0.137795 ft]; Pilot_Dia_4=21 mm  [stored 0.0688976 ft]; Pilot_Dia_5=14 mm  [stored 0.0459318 ft]; Pilot_top_1=638 mm; Pilot_top_ref=147 mm; Profile1_Height=430 mm; Profile1_Length=70 mm; Profile1_Length_2=47 mm; Profile_Dia=15 mm  [stored 0.0492126 ft]; Profile_Dia_2=15 mm  [stored 0.0492126 ft]; Profile_Dia_3=30 mm  [stored 0.0984252 ft]; Top_Profile=392 mm; Top_Profile_Ref=397 mm; W=600 mm; W_Ref=590 mm
- 879-0400-10-04400059999_DN400_PN10: 879-0050-10-14400059999=DN50_PN10/16; 879-0050-10-144000599A0=DN50_PN10/16; Body_Collar_Dia=115 mm; Body_Collar_Dia_2=99 mm; Body_Flange_Dia=355 mm; Body_Flange_Dia_2=393 mm; Body_Height_1=275 mm; Body_Height_2=138 mm; Body_Height_3=110 mm; Body_Height_4=153 mm; Body_Top_Dia=49 mm; Body_Top_Dia_2=41 mm; Body_With_Dia=275 mm; Body_With_Dia_2=297 mm; Bolt_support=733 mm; Bolt_support_2=367 mm; Bolt_support_Dia=40 mm  [stored 0.131234 ft]; Bolt_support_lenght=220 mm; Bolt_support_lenght_2=230 mm; Bottom_profile=100 mm; D1=240 mm; D3=283 mm; DN=400 mm; Fillet_Length=20 mm  [stored 0.0656168 ft]; Flange_thickness=28 mm  [stored 0.0918635 ft]; H3=1020 mm; ID=200 mm; L=1100 mm; PG_Dia=133 mm; PG_Ref=183 mm; PG_depth=28 mm  [stored 0.0918635 ft]; PG_ref=210 mm; Pilot_Dia_1=69 mm; Pilot_Dia_2=138 mm; Pilot_Dia_3=46 mm; Pilot_Dia_4=23 mm  [stored 0.0754593 ft]; Pilot_Dia_5=15 mm  [stored 0.0492126 ft]; Pilot_top_1=648 mm; Pilot_top_ref=90 mm; Profile1_Height=480 mm; Profile1_Length=76 mm; Profile1_Length_2=51 mm; Profile_Dia=20 mm  [stored 0.0656168 ft]; Profile_Dia_2=20 mm  [stored 0.0656168 ft]; Profile_Dia_3=40 mm  [stored 0.131234 ft]; Top_Profile=440 mm; Top_Profile_Ref=445 mm; W=660 mm; W_Ref=646 mm
- 879-0400-10-044000599A0_DN400_PN10: 879-0050-10-14400059999=DN50_PN10/16; 879-0050-10-144000599A0=DN50_PN10/16; Body_Collar_Dia=115 mm; Body_Collar_Dia_2=99 mm; Body_Flange_Dia=355 mm; Body_Flange_Dia_2=393 mm; Body_Height_1=275 mm; Body_Height_2=138 mm; Body_Height_3=122 mm; Body_Height_4=153 mm; Body_Top_Dia=49 mm; Body_Top_Dia_2=41 mm; Body_With_Dia=275 mm; Body_With_Dia_2=297 mm; Bolt_support=733 mm; Bolt_support_2=367 mm; Bolt_support_Dia=40 mm  [stored 0.131234 ft]; Bolt_support_lenght=220 mm; Bolt_support_lenght_2=230 mm; Bottom_profile=100 mm; D1=240 mm; D3=283 mm; DN=400 mm; Fillet_Length=20 mm  [stored 0.0656168 ft]; Flange_thickness=28 mm  [stored 0.0918635 ft]; H3=1183 mm; ID=200 mm; L=1100 mm; PG_Dia=133 mm; PG_Ref=183 mm; PG_depth=28 mm  [stored 0.0918635 ft]; PG_ref=210 mm; Pilot_Dia_1=69 mm; Pilot_Dia_2=138 mm; Pilot_Dia_3=46 mm; Pilot_Dia_4=23 mm  [stored 0.0754593 ft]; Pilot_Dia_5=15 mm  [stored 0.0492126 ft]; Pilot_top_1=735 mm; Pilot_top_ref=166 mm; Profile1_Height=480 mm; Profile1_Length=76 mm; Profile1_Length_2=51 mm; Profile_Dia=20 mm  [stored 0.0656168 ft]; Profile_Dia_2=20 mm  [stored 0.0656168 ft]; Profile_Dia_3=40 mm  [stored 0.131234 ft]; Top_Profile=440 mm; Top_Profile_Ref=445 mm; W=660 mm; W_Ref=646 mm
- 879-0400-10-14400059999_DN400_PN16: 879-0050-10-14400059999=DN50_PN10/16; 879-0050-10-144000599A0=DN50_PN10/16; Body_Collar_Dia=115 mm; Body_Collar_Dia_2=99 mm; Body_Flange_Dia=355 mm; Body_Flange_Dia_2=393 mm; Body_Height_1=275 mm; Body_Height_2=138 mm; Body_Height_3=100 mm; Body_Height_4=153 mm; Body_Top_Dia=49 mm; Body_Top_Dia_2=41 mm; Body_With_Dia=275 mm; Body_With_Dia_2=297 mm; Bolt_support=733 mm; Bolt_support_2=367 mm; Bolt_support_Dia=40 mm  [stored 0.131234 ft]; Bolt_support_lenght=220 mm; Bolt_support_lenght_2=230 mm; Bottom_profile=100 mm; D1=240 mm; D3=290 mm; DN=400 mm; Fillet_Length=20 mm  [stored 0.0656168 ft]; Flange_thickness=28 mm  [stored 0.0918635 ft]; H3=1020 mm; ID=200 mm; L=1100 mm; PG_Dia=133 mm; PG_Ref=183 mm; PG_depth=28 mm  [stored 0.0918635 ft]; PG_ref=210 mm; Pilot_Dia_1=71 mm; Pilot_Dia_2=142 mm; Pilot_Dia_3=47 mm; Pilot_Dia_4=24 mm; Pilot_Dia_5=16 mm  [stored 0.0524934 ft]; Pilot_top_1=639 mm; Pilot_top_ref=91 mm; Profile1_Height=480 mm; Profile1_Length=78 mm; Profile1_Length_2=52 mm; Profile_Dia=20 mm  [stored 0.0656168 ft]; Profile_Dia_2=20 mm  [stored 0.0656168 ft]; Profile_Dia_3=40 mm  [stored 0.131234 ft]; Top_Profile=440 mm; Top_Profile_Ref=445 mm; W=660 mm; W_Ref=646 mm
- 879-0400-10-144000599A0_DN400_PN16: 879-0050-10-14400059999=DN50_PN10/16; 879-0050-10-144000599A0=DN50_PN10/16; Body_Collar_Dia=115 mm; Body_Collar_Dia_2=99 mm; Body_Flange_Dia=355 mm; Body_Flange_Dia_2=393 mm; Body_Height_1=275 mm; Body_Height_2=138 mm; Body_Height_3=110 mm; Body_Height_4=153 mm; Body_Top_Dia=49 mm; Body_Top_Dia_2=41 mm; Body_With_Dia=275 mm; Body_With_Dia_2=297 mm; Bolt_support=733 mm; Bolt_support_2=367 mm; Bolt_support_Dia=40 mm  [stored 0.131234 ft]; Bolt_support_lenght=220 mm; Bolt_support_lenght_2=230 mm; Bottom_profile=100 mm; D1=240 mm; D3=290 mm; DN=400 mm; Fillet_Length=20 mm  [stored 0.0656168 ft]; Flange_thickness=28 mm  [stored 0.0918635 ft]; H3=1183 mm; ID=200 mm; L=1100 mm; PG_Dia=133 mm; PG_Ref=183 mm; PG_depth=28 mm  [stored 0.0918635 ft]; PG_ref=210 mm; Pilot_Dia_1=71 mm; Pilot_Dia_2=142 mm; Pilot_Dia_3=47 mm; Pilot_Dia_4=24 mm; Pilot_Dia_5=16 mm  [stored 0.0524934 ft]; Pilot_top_1=725 mm; Pilot_top_ref=168 mm; Profile1_Height=480 mm; Profile1_Length=78 mm; Profile1_Length_2=52 mm; Profile_Dia=20 mm  [stored 0.0656168 ft]; Profile_Dia_2=20 mm  [stored 0.0656168 ft]; Profile_Dia_3=40 mm  [stored 0.131234 ft]; Top_Profile=440 mm; Top_Profile_Ref=445 mm; W=660 mm; W_Ref=646 mm
- 879-0450-10-04400059999_DN450_PN10: 879-0050-10-14400059999=DN50_PN10/16; 879-0050-10-144000599A0=DN50_PN10/16; Body_Collar_Dia=125 mm; Body_Collar_Dia_2=108 mm; Body_Flange_Dia=387 mm; Body_Flange_Dia_2=429 mm; Body_Height_1=300 mm; Body_Height_2=150 mm; Body_Height_3=120 mm; Body_Height_4=165 mm; Body_Top_Dia=54 mm; Body_Top_Dia_2=45 mm; Body_With_Dia=300 mm; Body_With_Dia_2=324 mm; Bolt_support=800 mm; Bolt_support_2=400 mm; Bolt_support_Dia=40 mm  [stored 0.131234 ft]; Bolt_support_lenght=245 mm; Bolt_support_lenght_2=255 mm; Bottom_profile=113 mm; D1=265 mm; D3=308 mm; DN=450 mm; Fillet_Length=20 mm  [stored 0.0656168 ft]; Flange_thickness=30 mm  [stored 0.0984252 ft]; H3=1200 mm; ID=225 mm; L=1200 mm; PG_Dia=150 mm; PG_Ref=200 mm; PG_depth=28 mm  [stored 0.0918635 ft]; PG_ref=235 mm; Pilot_Dia_1=76 mm; Pilot_Dia_2=151 mm; Pilot_Dia_3=50 mm; Pilot_Dia_4=25 mm  [stored 0.082021 ft]; Pilot_Dia_5=17 mm; Pilot_top_1=749 mm; Pilot_top_ref=144 mm; Profile1_Height=509 mm; Profile1_Length=83 mm; Profile1_Length_2=55 mm; Profile_Dia=20 mm  [stored 0.0656168 ft]; Profile_Dia_2=20 mm  [stored 0.0656168 ft]; Profile_Dia_3=40 mm  [stored 0.131234 ft]; Top_Profile=480 mm; Top_Profile_Ref=485 mm; W=720 mm; W_Ref=706 mm
- 879-0450-10-044000599A0_DN450_PN10: 879-0050-10-14400059999=DN50_PN10/16; 879-0050-10-144000599A0=DN50_PN10/16; Body_Collar_Dia=125 mm; Body_Collar_Dia_2=108 mm; Body_Flange_Dia=387 mm; Body_Flange_Dia_2=429 mm; Body_Height_1=300 mm; Body_Height_2=150 mm; Body_Height_3=120 mm; Body_Height_4=165 mm; Body_Top_Dia=54 mm; Body_Top_Dia_2=45 mm; Body_With_Dia=300 mm; Body_With_Dia_2=324 mm; Bolt_support=800 mm; Bolt_support_2=400 mm; Bolt_support_Dia=40 mm  [stored 0.131234 ft]; Bolt_support_lenght=245 mm; Bolt_support_lenght_2=255 mm; Bottom_profile=113 mm; D1=265 mm; D3=308 mm; DN=450 mm; Fillet_Length=20 mm  [stored 0.0656168 ft]; Flange_thickness=30 mm  [stored 0.0984252 ft]; H3=1361 mm; ID=225 mm; L=1200 mm; PG_Dia=150 mm; PG_Ref=200 mm; PG_depth=28 mm  [stored 0.0918635 ft]; PG_ref=235 mm; Pilot_Dia_1=76 mm; Pilot_Dia_2=151 mm; Pilot_Dia_3=50 mm; Pilot_Dia_4=25 mm  [stored 0.082021 ft]; Pilot_Dia_5=17 mm; Pilot_top_1=829 mm; Pilot_top_ref=224 mm; Profile1_Height=531 mm; Profile1_Length=83 mm; Profile1_Length_2=55 mm; Profile_Dia=20 mm  [stored 0.0656168 ft]; Profile_Dia_2=20 mm  [stored 0.0656168 ft]; Profile_Dia_3=40 mm  [stored 0.131234 ft]; Top_Profile=480 mm; Top_Profile_Ref=485 mm; W=720 mm; W_Ref=706 mm
- 879-0450-10-14400059999_DN450_PN16: 879-0050-10-14400059999=DN50_PN10/16; 879-0050-10-144000599A0=DN50_PN10/16; Body_Collar_Dia=125 mm; Body_Collar_Dia_2=108 mm; Body_Flange_Dia=387 mm; Body_Flange_Dia_2=429 mm; Body_Height_1=300 mm; Body_Height_2=150 mm; Body_Height_3=120 mm; Body_Height_4=165 mm; Body_Top_Dia=54 mm; Body_Top_Dia_2=45 mm; Body_With_Dia=300 mm; Body_With_Dia_2=324 mm; Bolt_support=800 mm; Bolt_support_2=400 mm; Bolt_support_Dia=40 mm  [stored 0.131234 ft]; Bolt_support_lenght=245 mm; Bolt_support_lenght_2=255 mm; Bottom_profile=113 mm; D1=274 mm; D3=320 mm; DN=450 mm; Fillet_Length=20 mm  [stored 0.0656168 ft]; Flange_thickness=30 mm  [stored 0.0984252 ft]; H3=1200 mm; ID=225 mm; L=1200 mm; PG_Dia=150 mm; PG_Ref=200 mm; PG_depth=28 mm  [stored 0.0918635 ft]; PG_ref=235 mm; Pilot_Dia_1=79 mm; Pilot_Dia_2=158 mm; Pilot_Dia_3=53 mm; Pilot_Dia_4=26 mm; Pilot_Dia_5=18 mm; Pilot_top_1=743 mm; Pilot_top_ref=138 mm; Profile1_Height=530 mm; Profile1_Length=86 mm; Profile1_Length_2=58 mm; Profile_Dia=20 mm  [stored 0.0656168 ft]; Profile_Dia_2=20 mm  [stored 0.0656168 ft]; Profile_Dia_3=40 mm  [stored 0.131234 ft]; Top_Profile=480 mm; Top_Profile_Ref=485 mm; W=720 mm; W_Ref=706 mm
- 879-0450-10-144000599A0_DN450_PN16: 879-0050-10-14400059999=DN50_PN10/16; 879-0050-10-144000599A0=DN50_PN10/16; Body_Collar_Dia=125 mm; Body_Collar_Dia_2=108 mm; Body_Flange_Dia=387 mm; Body_Flange_Dia_2=429 mm; Body_Height_1=300 mm; Body_Height_2=150 mm; Body_Height_3=120 mm; Body_Height_4=165 mm; Body_Top_Dia=54 mm; Body_Top_Dia_2=45 mm; Body_With_Dia=300 mm; Body_With_Dia_2=324 mm; Bolt_support=800 mm; Bolt_support_2=400 mm; Bolt_support_Dia=40 mm  [stored 0.131234 ft]; Bolt_support_lenght=245 mm; Bolt_support_lenght_2=255 mm; Bottom_profile=113 mm; D1=274 mm; D3=320 mm; DN=450 mm; Fillet_Length=20 mm  [stored 0.0656168 ft]; Flange_thickness=30 mm  [stored 0.0984252 ft]; H3=1361 mm; ID=225 mm; L=1200 mm; PG_Dia=150 mm; PG_Ref=200 mm; PG_depth=28 mm  [stored 0.0918635 ft]; PG_ref=235 mm; Pilot_Dia_1=79 mm; Pilot_Dia_2=158 mm; Pilot_Dia_3=53 mm; Pilot_Dia_4=26 mm; Pilot_Dia_5=18 mm; Pilot_top_1=823 mm; Pilot_top_ref=218 mm; Profile1_Height=531 mm; Profile1_Length=86 mm; Profile1_Length_2=58 mm; Profile_Dia=20 mm  [stored 0.0656168 ft]; Profile_Dia_2=20 mm  [stored 0.0656168 ft]; Profile_Dia_3=40 mm  [stored 0.131234 ft]; Top_Profile=480 mm; Top_Profile_Ref=485 mm; W=720 mm; W_Ref=706 mm
- 879-0500-10-04400059999_DN500_PN10: 879-0050-10-14400059999=DN50_PN10/16; 879-0050-10-144000599A0=DN50_PN10/16; Body_Collar_Dia=130 mm; Body_Collar_Dia_2=112 mm; Body_Flange_Dia=403 mm; Body_Flange_Dia_2=446 mm; Body_Height_1=313 mm; Body_Height_2=156 mm; Body_Height_3=125 mm; Body_Height_4=171 mm; Body_Top_Dia=56 mm; Body_Top_Dia_2=47 mm; Body_With_Dia=313 mm; Body_With_Dia_2=338 mm; Bolt_support=833 mm; Bolt_support_2=417 mm; Bolt_support_Dia=50 mm; Bolt_support_lenght=270 mm; Bolt_support_lenght_2=280 mm; Bottom_profile=125 mm; D1=291 mm; D3=335 mm; DN=500 mm; Fillet_Length=25 mm  [stored 0.082021 ft]; Flange_thickness=32 mm; H3=1270 mm; ID=250 mm; L=1250 mm; PG_Dia=167 mm; PG_Ref=208 mm; PG_depth=35 mm  [stored 0.114829 ft]; PG_ref=260 mm; Pilot_Dia_1=83 mm; Pilot_Dia_2=166 mm; Pilot_Dia_3=55 mm; Pilot_Dia_4=28 mm  [stored 0.0918635 ft]; Pilot_Dia_5=18 mm; Pilot_top_1=782 mm; Pilot_top_ref=153 mm; Profile1_Height=541 mm; Profile1_Length=91 mm; Profile1_Length_2=60 mm; Profile_Dia=25 mm  [stored 0.082021 ft]; Profile_Dia_2=25 mm  [stored 0.082021 ft]; Profile_Dia_3=50 mm; Top_Profile=500 mm; Top_Profile_Ref=505 mm; W=795 mm; W_Ref=778 mm
- 879-0500-10-044000599A0_DN500_PN10: 879-0050-10-14400059999=DN50_PN10/16; 879-0050-10-144000599A0=DN50_PN10/16; Body_Collar_Dia=130 mm; Body_Collar_Dia_2=112 mm; Body_Flange_Dia=403 mm; Body_Flange_Dia_2=446 mm; Body_Height_1=313 mm; Body_Height_2=156 mm; Body_Height_3=125 mm; Body_Height_4=171 mm; Body_Top_Dia=56 mm; Body_Top_Dia_2=47 mm; Body_With_Dia=313 mm; Body_With_Dia_2=338 mm; Bolt_support=833 mm; Bolt_support_2=417 mm; Bolt_support_Dia=50 mm; Bolt_support_lenght=270 mm; Bolt_support_lenght_2=280 mm; Bottom_profile=125 mm; D1=291 mm; D3=335 mm; DN=500 mm; Fillet_Length=25 mm  [stored 0.082021 ft]; Flange_thickness=32 mm; H3=1435 mm; ID=250 mm; L=1250 mm; PG_Dia=167 mm; PG_Ref=208 mm; PG_depth=35 mm  [stored 0.114829 ft]; PG_ref=260 mm; Pilot_Dia_1=83 mm; Pilot_Dia_2=166 mm; Pilot_Dia_3=55 mm; Pilot_Dia_4=28 mm  [stored 0.0918635 ft]; Pilot_Dia_5=18 mm; Pilot_top_1=864 mm; Pilot_top_ref=236 mm; Profile1_Height=541 mm; Profile1_Length=91 mm; Profile1_Length_2=60 mm; Profile_Dia=25 mm  [stored 0.082021 ft]; Profile_Dia_2=25 mm  [stored 0.082021 ft]; Profile_Dia_3=50 mm; Top_Profile=500 mm; Top_Profile_Ref=505 mm; W=795 mm; W_Ref=778 mm
- 879-0500-10-14400059999_DN500_PN16: 879-0050-10-14400059999=DN50_PN10/16; 879-0050-10-144000599A0=DN50_PN10/16; Body_Collar_Dia=130 mm; Body_Collar_Dia_2=112 mm; Body_Flange_Dia=403 mm; Body_Flange_Dia_2=446 mm; Body_Height_1=313 mm; Body_Height_2=156 mm; Body_Height_3=125 mm; Body_Height_4=171 mm; Body_Top_Dia=56 mm; Body_Top_Dia_2=47 mm; Body_With_Dia=313 mm; Body_With_Dia_2=338 mm; Bolt_support=833 mm; Bolt_support_2=417 mm; Bolt_support_Dia=50 mm; Bolt_support_lenght=270 mm; Bolt_support_lenght_2=280 mm; Bottom_profile=125 mm; D1=305 mm; D3=358 mm; DN=500 mm; Fillet_Length=25 mm  [stored 0.082021 ft]; Flange_thickness=32 mm; H3=1270 mm; ID=250 mm; L=1250 mm; PG_Dia=167 mm; PG_Ref=208 mm; PG_depth=35 mm  [stored 0.114829 ft]; PG_ref=260 mm; Pilot_Dia_1=89 mm; Pilot_Dia_2=178 mm; Pilot_Dia_3=59 mm; Pilot_Dia_4=30 mm  [stored 0.0984252 ft]; Pilot_Dia_5=20 mm  [stored 0.0656168 ft]; Pilot_top_1=771 mm; Pilot_top_ref=142 mm; Profile1_Height=541 mm; Profile1_Length=97 mm; Profile1_Length_2=64 mm; Profile_Dia=25 mm  [stored 0.082021 ft]; Profile_Dia_2=25 mm  [stored 0.082021 ft]; Profile_Dia_3=50 mm; Top_Profile=500 mm; Top_Profile_Ref=505 mm; W=795 mm; W_Ref=778 mm
- 879-0500-10-144000599A0_DN500_PN16: 879-0050-10-14400059999=DN50_PN10/16; 879-0050-10-144000599A0=DN50_PN10/16; Body_Collar_Dia=130 mm; Body_Collar_Dia_2=112 mm; Body_Flange_Dia=403 mm; Body_Flange_Dia_2=446 mm; Body_Height_1=313 mm; Body_Height_2=156 mm; Body_Height_3=125 mm; Body_Height_4=171 mm; Body_Top_Dia=56 mm; Body_Top_Dia_2=47 mm; Body_With_Dia=313 mm; Body_With_Dia_2=338 mm; Bolt_support=833 mm; Bolt_support_2=417 mm; Bolt_support_Dia=50 mm; Bolt_support_lenght=270 mm; Bolt_support_lenght_2=280 mm; Bottom_profile=125 mm; D1=305 mm; D3=358 mm; DN=500 mm; Fillet_Length=25 mm  [stored 0.082021 ft]; Flange_thickness=32 mm; H3=1435 mm; ID=250 mm; L=1250 mm; PG_Dia=167 mm; PG_Ref=208 mm; PG_depth=35 mm  [stored 0.114829 ft]; PG_ref=260 mm; Pilot_Dia_1=89 mm; Pilot_Dia_2=178 mm; Pilot_Dia_3=59 mm; Pilot_Dia_4=30 mm  [stored 0.0984252 ft]; Pilot_Dia_5=20 mm  [stored 0.0656168 ft]; Pilot_top_1=853 mm; Pilot_top_ref=224 mm; Profile1_Height=563 mm; Profile1_Length=97 mm; Profile1_Length_2=64 mm; Profile_Dia=25 mm  [stored 0.082021 ft]; Profile_Dia_2=25 mm  [stored 0.082021 ft]; Profile_Dia_3=50 mm; Top_Profile=500 mm; Top_Profile_Ref=505 mm; W=795 mm; W_Ref=778 mm
- 879-0600-10-04400059999_DN600_PN10: 879-0050-10-14400059999=DN50_PN10/16; 879-0050-10-144000599A0=DN50_PN10/16; Body_Collar_Dia=151 mm; Body_Collar_Dia_2=130 mm; Body_Flange_Dia=468 mm; Body_Flange_Dia_2=518 mm; Body_Height_1=363 mm; Body_Height_2=181 mm; Body_Height_3=145 mm; Body_Height_4=196 mm; Body_Top_Dia=65 mm; Body_Top_Dia_2=54 mm; Body_With_Dia=363 mm; Body_With_Dia_2=392 mm; Bolt_support=967 mm; Bolt_support_2=483 mm; Bolt_support_Dia=60 mm; Bolt_support_lenght=320 mm; Bolt_support_lenght_2=330 mm; Bottom_profile=150 mm; D1=341 mm; D3=390 mm; DN=600 mm; Fillet_Length=30 mm  [stored 0.0984252 ft]; Flange_thickness=36 mm  [stored 0.11811 ft]; H3=1420 mm; ID=300 mm; L=1450 mm; PG_Dia=200 mm; PG_Ref=242 mm; PG_depth=42 mm  [stored 0.137795 ft]; PG_ref=310 mm; Pilot_Dia_1=98 mm; Pilot_Dia_2=196 mm; Pilot_Dia_3=65 mm; Pilot_Dia_4=33 mm; Pilot_Dia_5=22 mm  [stored 0.0721785 ft]; Pilot_top_1=877 mm; Pilot_top_ref=153 mm; Profile1_Height=616 mm; Profile1_Length=105 mm; Profile1_Length_2=70 mm; Profile_Dia=30 mm  [stored 0.0984252 ft]; Profile_Dia_2=30 mm  [stored 0.0984252 ft]; Profile_Dia_3=60 mm; Top_Profile=580 mm; Top_Profile_Ref=585 mm; W=920 mm; W_Ref=899 mm
- 879-0600-10-044000599A0_DN600_PN10: 879-0050-10-14400059999=DN50_PN10/16; 879-0050-10-144000599A0=DN50_PN10/16; Body_Collar_Dia=151 mm; Body_Collar_Dia_2=130 mm; Body_Flange_Dia=468 mm; Body_Flange_Dia_2=518 mm; Body_Height_1=363 mm; Body_Height_2=181 mm; Body_Height_3=145 mm; Body_Height_4=196 mm; Body_Top_Dia=65 mm; Body_Top_Dia_2=54 mm; Body_With_Dia=363 mm; Body_With_Dia_2=392 mm; Bolt_support=967 mm; Bolt_support_2=483 mm; Bolt_support_Dia=60 mm; Bolt_support_lenght=320 mm; Bolt_support_lenght_2=330 mm; Bottom_profile=150 mm; D1=341 mm; D3=390 mm; DN=600 mm; Fillet_Length=30 mm  [stored 0.0984252 ft]; Flange_thickness=36 mm  [stored 0.11811 ft]; H3=1584 mm; ID=300 mm; L=1450 mm; PG_Dia=200 mm; PG_Ref=242 mm; PG_depth=42 mm  [stored 0.137795 ft]; PG_ref=310 mm; Pilot_Dia_1=98 mm; Pilot_Dia_2=196 mm; Pilot_Dia_3=65 mm; Pilot_Dia_4=33 mm; Pilot_Dia_5=22 mm  [stored 0.0721785 ft]; Pilot_top_1=959 mm; Pilot_top_ref=235 mm; Profile1_Height=660 mm; Profile1_Length=105 mm; Profile1_Length_2=70 mm; Profile_Dia=30 mm  [stored 0.0984252 ft]; Profile_Dia_2=30 mm  [stored 0.0984252 ft]; Profile_Dia_3=60 mm; Top_Profile=580 mm; Top_Profile_Ref=585 mm; W=920 mm; W_Ref=899 mm
- 879-0600-10-14400059999_DN600_PN16: 879-0050-10-14400059999=DN50_PN10/16; 879-0050-10-144000599A0=DN50_PN10/16; Body_Collar_Dia=151 mm; Body_Collar_Dia_2=130 mm; Body_Flange_Dia=468 mm; Body_Flange_Dia_2=518 mm; Body_Height_1=363 mm; Body_Height_2=181 mm; Body_Height_3=145 mm; Body_Height_4=196 mm; Body_Top_Dia=65 mm; Body_Top_Dia_2=54 mm; Body_With_Dia=363 mm; Body_With_Dia_2=392 mm; Bolt_support=967 mm; Bolt_support_2=483 mm; Bolt_support_Dia=60 mm; Bolt_support_lenght=320 mm; Bolt_support_lenght_2=330 mm; Bottom_profile=150 mm; D1=360 mm; D3=420 mm; DN=600 mm; Fillet_Length=30 mm  [stored 0.0984252 ft]; Flange_thickness=36 mm  [stored 0.11811 ft]; H3=1420 mm; ID=300 mm; L=1450 mm; PG_Dia=200 mm; PG_Ref=242 mm; PG_depth=42 mm  [stored 0.137795 ft]; PG_ref=310 mm; Pilot_Dia_1=106 mm; Pilot_Dia_2=212 mm; Pilot_Dia_3=71 mm; Pilot_Dia_4=35 mm  [stored 0.114829 ft]; Pilot_Dia_5=24 mm; Pilot_top_1=862 mm; Pilot_top_ref=138 mm; Profile1_Height=616 mm; Profile1_Length=114 mm; Profile1_Length_2=76 mm; Profile_Dia=30 mm  [stored 0.0984252 ft]; Profile_Dia_2=30 mm  [stored 0.0984252 ft]; Profile_Dia_3=60 mm; Top_Profile=580 mm; Top_Profile_Ref=585 mm; W=920 mm; W_Ref=899 mm
- 879-0600-10-144000599A0_DN600_PN16: 879-0050-10-14400059999=DN50_PN10/16; 879-0050-10-144000599A0=DN50_PN10/16; Body_Collar_Dia=151 mm; Body_Collar_Dia_2=130 mm; Body_Flange_Dia=468 mm; Body_Flange_Dia_2=518 mm; Body_Height_1=363 mm; Body_Height_2=181 mm; Body_Height_3=145 mm; Body_Height_4=196 mm; Body_Top_Dia=65 mm; Body_Top_Dia_2=54 mm; Body_With_Dia=363 mm; Body_With_Dia_2=392 mm; Bolt_support=967 mm; Bolt_support_2=483 mm; Bolt_support_Dia=60 mm; Bolt_support_lenght=320 mm; Bolt_support_lenght_2=330 mm; Bottom_profile=150 mm; D1=360 mm; D3=420 mm; DN=600 mm; Fillet_Length=30 mm  [stored 0.0984252 ft]; Flange_thickness=36 mm  [stored 0.11811 ft]; H3=1584 mm; ID=300 mm; L=1450 mm; PG_Dia=200 mm; PG_Ref=242 mm; PG_depth=42 mm  [stored 0.137795 ft]; PG_ref=310 mm; Pilot_Dia_1=106 mm; Pilot_Dia_2=212 mm; Pilot_Dia_3=71 mm; Pilot_Dia_4=35 mm  [stored 0.114829 ft]; Pilot_Dia_5=24 mm; Pilot_top_1=944 mm; Pilot_top_ref=220 mm; Profile1_Height=660 mm; Profile1_Length=114 mm; Profile1_Length_2=76 mm; Profile_Dia=30 mm  [stored 0.0984252 ft]; Profile_Dia_2=30 mm  [stored 0.0984252 ft]; Profile_Dia_3=60 mm; Top_Profile=580 mm; Top_Profile_Ref=585 mm; W=920 mm; W_Ref=899 mm
- 879-0050-10-14400059999_DN50_PN10/16: 879-0050-10-14400059999=DN50_PN10/16; 879-0050-10-144000599A0=DN50_PN10/16; Body_Collar_Dia=24 mm; Body_Collar_Dia_2=21 mm  [stored 0.0688976 ft]; Body_Flange_Dia=74 mm; Body_Flange_Dia_2=82 mm; Body_Height_1=58 mm; Body_Height_2=29 mm; Body_Height_3=45 mm; Body_Height_4=44 mm; Body_Top_Dia=10 mm  [stored 0.0328084 ft]; Body_Top_Dia_2=9 mm  [stored 0.0295276 ft]; Body_With_Dia=58 mm; Body_With_Dia_2=62 mm; Bolt_support=153 mm; Bolt_support_2=77 mm; Bolt_support_Dia=12 mm  [stored 0.0393701 ft]; Bolt_support_lenght=45 mm; Bolt_support_lenght_2=55 mm; Bottom_profile=13 mm; D1=50 mm; D3=83 mm; DN=50 mm; Fillet_Length=6 mm  [stored 0.019685 ft]; Flange_thickness=19 mm  [stored 0.062336 ft]; H3=370 mm; ID=25 mm  [stored 0.082021 ft]; L=230 mm; PG_Dia=25 mm  [stored 0.082021 ft]; PG_Ref=38 mm; PG_depth=8 mm  [stored 0.0262467 ft]; PG_ref=35 mm  [stored 0.114829 ft]; Pilot_Dia_1=15 mm  [stored 0.0492126 ft]; Pilot_Dia_2=30 mm  [stored 0.0984252 ft]; Pilot_Dia_3=10 mm  [stored 0.0328084 ft]; Pilot_Dia_4=5 mm  [stored 0.0164042 ft]; Pilot_Dia_5=3 mm  [stored 0.00984252 ft]; Pilot_top_1=227 mm; Pilot_top_ref=61 mm; Profile1_Height=135 mm; Profile1_Length=22 mm  [stored 0.0721785 ft]; Profile1_Length_2=15 mm  [stored 0.0492126 ft]; Profile_Dia=6 mm  [stored 0.019685 ft]; Profile_Dia_2=6 mm  [stored 0.019685 ft]; Profile_Dia_3=12 mm  [stored 0.0393701 ft]; Top_Profile=92 mm; Top_Profile_Ref=97 mm; W=266 mm; W_Ref=262 mm
- 879-0050-10-144000599A0_DN50_PN10/16: 879-0050-10-14400059999=DN125_PN10/16; 879-0050-10-144000599A0=DN125_PN10/16; Body_Collar_Dia=24 mm; Body_Collar_Dia_2=21 mm  [stored 0.0688976 ft]; Body_Flange_Dia=74 mm; Body_Flange_Dia_2=82 mm; Body_Height_1=58 mm; Body_Height_2=29 mm; Body_Height_3=50 mm; Body_Height_4=44 mm; Body_Top_Dia=10 mm  [stored 0.0328084 ft]; Body_Top_Dia_2=9 mm  [stored 0.0295276 ft]; Body_With_Dia=58 mm; Body_With_Dia_2=62 mm; Bolt_support=153 mm; Bolt_support_2=77 mm; Bolt_support_Dia=12 mm  [stored 0.0393701 ft]; Bolt_support_lenght=45 mm; Bolt_support_lenght_2=55 mm; Bottom_profile=13 mm; D1=50 mm; D3=83 mm; DN=50 mm; Fillet_Length=6 mm  [stored 0.019685 ft]; Flange_thickness=19 mm  [stored 0.062336 ft]; H3=407 mm; ID=25 mm  [stored 0.082021 ft]; L=230 mm; PG_Dia=25 mm  [stored 0.082021 ft]; PG_Ref=38 mm; PG_depth=8 mm  [stored 0.0262467 ft]; PG_ref=35 mm  [stored 0.114829 ft]; Pilot_Dia_1=15 mm  [stored 0.0492126 ft]; Pilot_Dia_2=30 mm  [stored 0.0984252 ft]; Pilot_Dia_3=10 mm  [stored 0.0328084 ft]; Pilot_Dia_4=5 mm  [stored 0.0164042 ft]; Pilot_Dia_5=3 mm  [stored 0.00984252 ft]; Pilot_top_1=248 mm; Pilot_top_ref=77 mm; Profile1_Height=145 mm; Profile1_Length=22 mm  [stored 0.0721785 ft]; Profile1_Length_2=15 mm  [stored 0.0492126 ft]; Profile_Dia=6 mm  [stored 0.019685 ft]; Profile_Dia_2=6 mm  [stored 0.019685 ft]; Profile_Dia_3=12 mm  [stored 0.0393701 ft]; Top_Profile=92 mm; Top_Profile_Ref=97 mm; W=266 mm; W_Ref=262 mm

note: [stored X ft] marks values corroborated as IEEE doubles in the binary element streams (Revit-internal decimal feet)

## geometry (parser evidence)
native form markers: Sweep x5
no freeform markers — native parametric forms only
